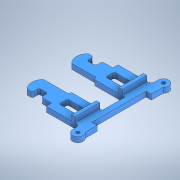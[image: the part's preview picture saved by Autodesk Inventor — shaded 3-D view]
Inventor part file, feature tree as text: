
AUTODESK INVENTOR PART (.ipt)
format: ipt  version: 2022 (Build 260153000, 153)  size: 316,928 bytes
history: native  units: in
note: dims shown in document units (in); Inventor stores cm internally (conversion verified against a paired STEP export)
features: extrude x5, sketch x5, mirror x3
ambient origin geometry x8: Origin, YZ Plane, XZ Plane, XY Plane, X Axis, Y Axis, Z Axis, Center Point
bodies: Solid1 (feature_tree)
feature tree (13):
  extrude  "Extrusion1"  TaperAngle=0.0deg  [1 undecoded]
  mirror  "Mirror1"
  extrude  "Extrusion2"  Depth=0.1969in
  mirror  "Mirror2"
  extrude  "Extrusion3"  Depth=0.1378in
  extrude  "Extrusion4"  Depth=0.0787in
  extrude  "Extrusion5"  Depth=0.0787in
  mirror  "Mirror3"
  sketch  "Sketch1"  dims[d1=0.8071in d2=0.0in]
  sketch  "Sketch2"  dims[d3=0.4724in d4=0.1969in]
  sketch  "Sketch3"  dims[d5=0.1832in d6=0.1378in]
  sketch  "Sketch5"  dims[d7=0.0787in d8=0.0787in]
  sketch  "Sketch6"  dims[d9=0.0787in d10=0.0787in d11=0.0394in d12=0.0394in d13=0.0394in d14=0.0394in d15=0.0394in d16=0.0394in d17=0.0394in d18=0.0394in d19=0.1575in d20=0.0787in d21=0.563in d22=0.7087in d23=0.1181in d24=0.374in d25=0.3765in d26=0.5118in d27=0.0709in d28=0.1969in d29=0.3346in d30=0.0787in d31=0.0787in d32=0.0787in d33=0.0787in d34=0.0394in d35=0.0394in d36=0.0394in d37=0.0394in d38=0.0394in d39=0.0394in d40=0.0394in d41=0.0394in d42=0.1181in d43=0.0in d44=0.0787in d46=0.1575in d47=0.2362in d48=0.2362in d49=0.1575in d50=0.0787in d51=0.2441in d52=0.1181in d53=0.0in d54=1.2205in d55=0.0in d56=0.6102in d57=0.1181in d58=0.1181in d59=0.0in d60=0.5118in d61=0.2559in d62=0.1181in d63=0.0in d64=0.9646in d65=0.0591in d66=0.0in d67=0.1181in d68=0.0in]
note: 1 required parameter value undecoded (feature->parameter linkage not recoverable at this tier; creation-order binding heuristic only, values carry confidence <= 0.55)
